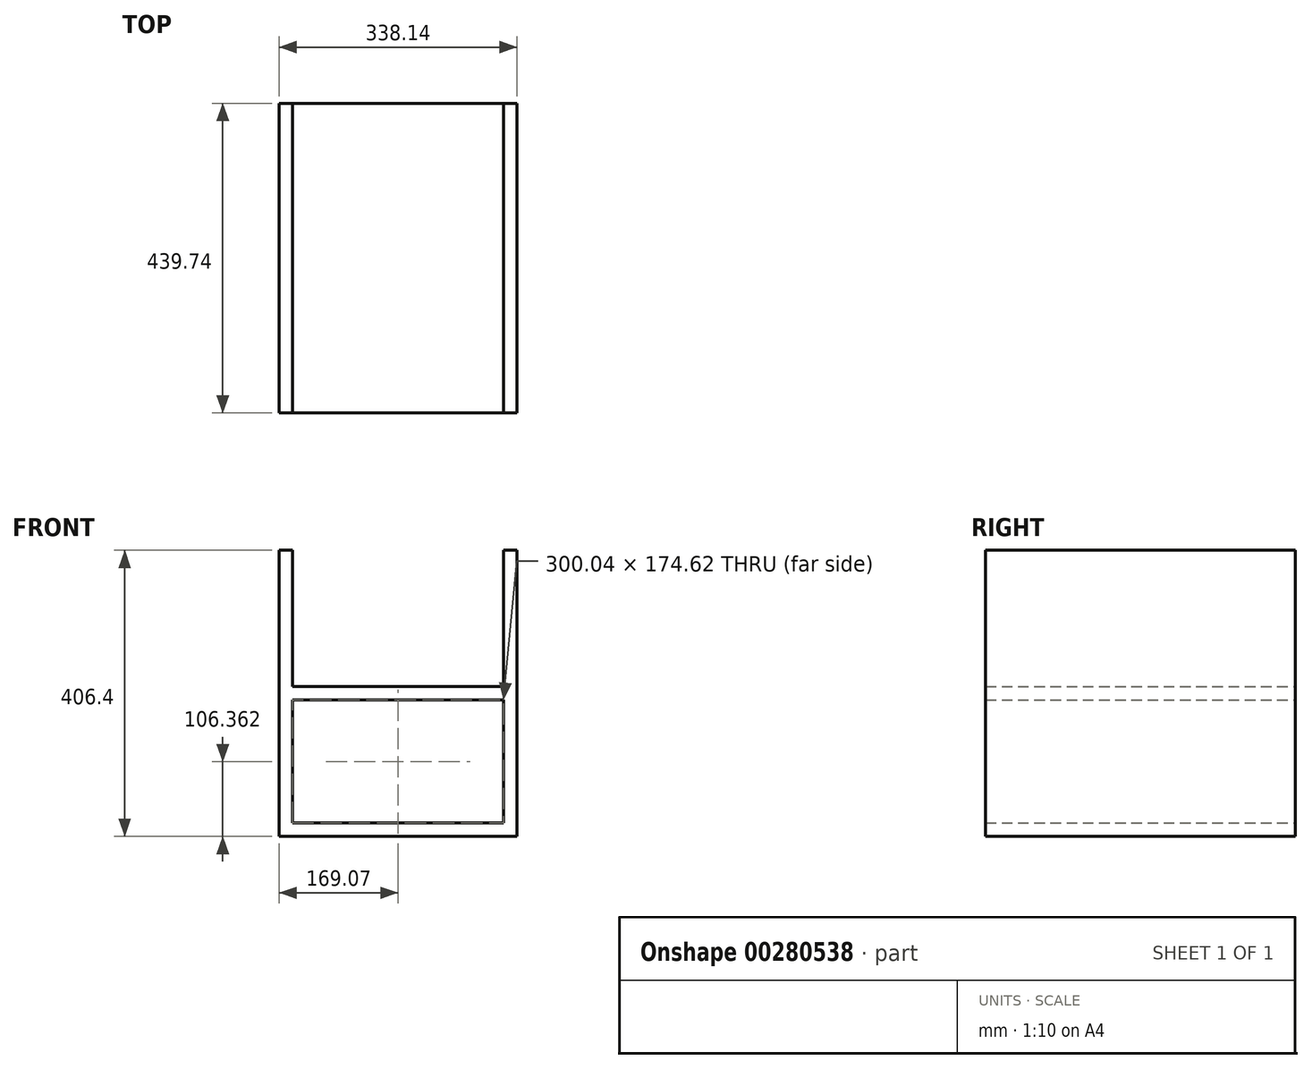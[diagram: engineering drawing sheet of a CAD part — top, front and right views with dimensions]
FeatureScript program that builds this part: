
annotation { "Feature Type Name" : "Feature", "Feature Type Description" : "" }
export const myFeature = defineFeature(function(context is Context, id is Id, definition is map)
    precondition{}
    {
        {
            var Q0;
            Q0=qCreatedBy(makeId("Front.planeOp"),FACE);
            var sketch = newSketch(context, id + "F0", { "sketchPlane" : qUnion([Q0])});
            skLineSegment(sketch, "E0.bottom", {"start": v(169.07, 203.2) * mm, "end": v(150.02, 203.2) * mm});
            skLineSegment(sketch, "E0.top", {"start": v(169.07, -203.2) * mm, "end": v(-169.07, -203.2) * mm});
            skLineSegment(sketch, "E0.left", {"start": v(169.07, 203.2) * mm, "end": v(169.07, -203.2) * mm});
            skLineSegment(sketch, "E0.right", {"start": v(-169.07, 203.2) * mm, "end": v(-169.07, -203.2) * mm});
            skPoint(sketch, "E0.middle", {"position": v(0, 0) * mm});
            skLineSegment(sketch, "E1.top", {"start": v(150.02, -184.15) * mm, "end": v(-150.02, -184.15) * mm});
            skLineSegment(sketch, "E1.left", {"start": v(150.02, 203.2) * mm, "end": v(150.02, 9.53) * mm});
            skLineSegment(sketch, "E1.right", {"start": v(-150.02, 203.2) * mm, "end": v(-150.02, 9.52) * mm});
            skLineSegment(sketch, "E2.bottom", {"start": v(150.02, 9.53) * mm, "end": v(-150.02, 9.52) * mm});
            skLineSegment(sketch, "E2.top", {"start": v(150.02, -9.52) * mm, "end": v(-150.02, -9.53) * mm});
            skLineSegment(sketch, "E3.trimOffspring", {"start": v(-150.02, -9.53) * mm, "end": v(-150.02, -184.15) * mm});
            skLineSegment(sketch, "E4.trimOffspring", {"start": v(150.02, -9.52) * mm, "end": v(150.02, -184.15) * mm});
            skPoint(sketch, "E5.orphan", {"position": v(150.02, 184.15) * mm});
            skPoint(sketch, "E6.orphan", {"position": v(-150.02, 184.15) * mm});
            skLineSegment(sketch, "E7.trimOffspring", {"start": v(-150.02, 203.2) * mm, "end": v(-169.07, 203.2) * mm});
            skSolve(sketch);
        }
        {
            var Q0;
            Q0=makeQuery(id+"F0.imprint","IMPRINT",FACE,{"disambiguationData":[TD([[makeQuery(id+"F0.imprint","IMPRINT",EDGE,{"derivedFrom":sQuery(id+"F0.wireOp",EDGE,"E0.bottom")}),1.0]])]});
            extrude(context, id + "F1", {"entities" : qUnion([Q0]), "depth" : 439.74 * mm});
        }
    });
